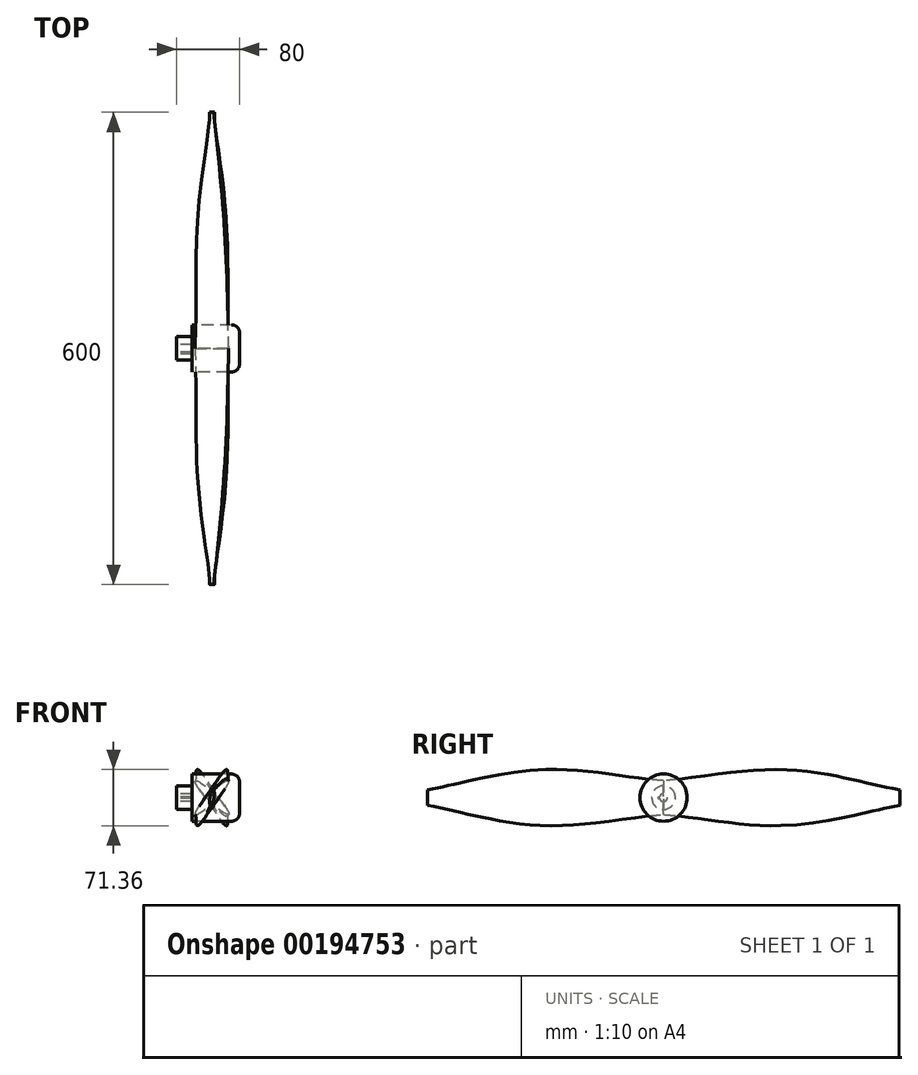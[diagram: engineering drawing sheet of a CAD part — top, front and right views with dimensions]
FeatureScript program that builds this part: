
annotation { "Feature Type Name" : "Feature", "Feature Type Description" : "" }
export const myFeature = defineFeature(function(context is Context, id is Id, definition is map)
    precondition{}
    {
        {
            assignVariable(context, id + "F0", {"name" : "Amplitude", "anyValue" : 300});
        }
        {
            var Q0;
            Q0=qCreatedBy(makeId("Front.planeOp"),FACE);
            var sketch = newSketch(context, id + "F1", { "sketchPlane" : qUnion([Q0])});
            skEllipse(sketch, "E0", {"center": v(0, 0) * mm, "majorRadius": 30 * mm, "minorRadius": 5 * mm, "majorAxis": v(0.7, 0.7)});
            skLineSegment(sketch, "E1", {"start": v(-21.21, -21.21) * mm, "end": v(21.21, 21.21) * mm, "construction": true});
            skLineSegment(sketch, "E2", {"start": v(-3.54, 3.54) * mm, "end": v(3.54, -3.54) * mm, "construction": true});
            skSolve(sketch);
        }
        {
            var Q0;
            Q0=qCreatedBy(makeId("Front.planeOp"),FACE);
            cPlane(context, id + "F2", {"entities" : qUnion([Q0]), "cplaneType" : CPlaneType.OFFSET, "offset" : (getVariable(context, 'Amplitude') / 2) * mm, "width" : 150 * mm, "height" : 150 * mm});
        }
        {
            var Q0;
            Q0=qCreatedBy(id+"F2.planeOp",FACE);
            var sketch = newSketch(context, id + "F3", { "sketchPlane" : qUnion([Q0])});
            skEllipse(sketch, "E3", {"center": v(0, 0) * mm, "majorRadius": 40 * mm, "minorRadius": 5 * mm, "majorAxis": v(0.46, 0.89)});
            skLineSegment(sketch, "E4", {"start": v(-18.47, -35.48) * mm, "end": v(18.47, 35.48) * mm, "construction": true});
            skLineSegment(sketch, "E5", {"start": v(4.44, -2.3) * mm, "end": v(-4.44, 2.3) * mm, "construction": true});
            skSolve(sketch);
        }
        {
            var Q0;
            Q0=qCreatedBy(makeId("Front.planeOp"),FACE);
            cPlane(context, id + "F4", {"entities" : qUnion([Q0]), "cplaneType" : CPlaneType.OFFSET, "offset" : (getVariable(context, 'Amplitude')) * mm, "width" : 150 * mm, "height" : 150 * mm});
        }
        {
            var Q0;
            Q0=qCreatedBy(id+"F4.planeOp",FACE);
            var sketch = newSketch(context, id + "F5", { "sketchPlane" : qUnion([Q0])});
            skEllipse(sketch, "E6", {"center": v(0, 0) * mm, "majorRadius": 10 * mm, "minorRadius": 2.5 * mm, "majorAxis": v(0.17, 0.98)});
            skLineSegment(sketch, "E7", {"start": v(-1.74, -9.85) * mm, "end": v(1.74, 9.85) * mm, "construction": true});
            skLineSegment(sketch, "E8", {"start": v(-2.46, 0.43) * mm, "end": v(2.46, -0.43) * mm, "construction": true});
            skSolve(sketch);
        }
        {
            var Q0;
            Q0 = qSketchRegion(id + "F1", true);
            var Q1;
            Q1 = qSketchRegion(id + "F3", true);
            var Q2;
            Q2 = qSketchRegion(id + "F5", true);
            loft(context, id + "F6", {"sheetProfilesArray" : [{ "sheetProfileEntities" : qUnion([Q0]) }, { "sheetProfileEntities" : qUnion([Q1]) }, { "sheetProfileEntities" : qUnion([Q2]) }]});
        }
        {
            var Q0;
            Q0=qCreatedBy(makeId("Front.planeOp"),FACE);
            var sketch = newSketch(context, id + "F7", { "sketchPlane" : qUnion([Q0])});
            skLineSegment(sketch, "E9", {"start": v(-110.8, 0) * mm, "end": v(122.07, 0) * mm, "construction": true});
            skSolve(sketch);
        }
        {
            var Q0;
            Q0=makeQuery(id+"F6.opLoft","SWEPT_BODY",BODY,{"disambiguationData":[OSD([makeQuery(id+"F1.imprint","IMPRINT",FACE,{"disambiguationData":[TD([[makeQuery(id+"F1.imprint","IMPRINT",EDGE,{"derivedFrom":sQuery(id+"F1.wireOp",EDGE,"E0")}),1.0]])]}),sQuery(id+"F3.wireOp",EDGE,"E3"),makeQuery(id+"F5.imprint","IMPRINT",FACE,{"disambiguationData":[TD([[makeQuery(id+"F5.imprint","IMPRINT",EDGE,{"derivedFrom":sQuery(id+"F5.wireOp",EDGE,"E6")}),1.0]])]})])]});
            var Q1;
            Q1=sQuery(id+"F7.wireOp",EDGE,"E9");
            circularPattern(context, id + "F8", {"entities" : qUnion([Q0]), "axis" : qUnion([Q1]), "angle" : 360 * degree, "instanceCount" : 2, "equalSpace" : true});
        }
        {
            var Q0;
            Q0=qCreatedBy(makeId("Front.planeOp"),FACE);
            var sketch = newSketch(context, id + "F9", { "sketchPlane" : qUnion([Q0])});
            skLineSegment(sketch, "E10", {"start": v(-45, 0) * mm, "end": v(35, 0) * mm});
            skLineSegment(sketch, "E11", {"start": v(35, 0) * mm, "end": v(35, 30) * mm});
            skLineSegment(sketch, "E12", {"start": v(35, 30) * mm, "end": v(-25, 30) * mm});
            skLineSegment(sketch, "E13", {"start": v(-25, 30) * mm, "end": v(-25, 15) * mm});
            skLineSegment(sketch, "E14", {"start": v(-25, 15) * mm, "end": v(-45, 15) * mm});
            skLineSegment(sketch, "E15", {"start": v(-45, 15) * mm, "end": v(-45, 0) * mm});
            skLineSegment(sketch, "E16", {"start": v(-48.47, 0) * mm, "end": v(48.08, 0) * mm, "construction": true});
            skSolve(sketch);
        }
        {
            var Q0;
            Q0 = qSketchRegion(id + "F9", true);
            var Q1;
            Q1=sQuery(id+"F9.wireOp",EDGE,"E16");
            revolve(context, id + "F10", {"entities" : qUnion([Q0]), "axis" : qUnion([Q1]), "revolveType" : RevolveType.FULL});
        }
        {
            var Q0;
            Q0=makeQuery(id+"F10.opRevolve","SWEPT_EDGE",EDGE,{"disambiguationData":[OSD([sQuery(id+"F9.wireOp",EDGE,"E11"),sQuery(id+"F9.wireOp",EDGE,"E12")])]});
            fillet(context, id + "F11", {"entities" : qUnion([Q0]), "radius" : 10 * mm, "tangentPropagation" : true, "allowEdgeOverflow" : false});
        }
        {
            var Q0;
            Q0=makeQuery(id+"F10.opRevolve","SWEPT_FACE",FACE,{"disambiguationData":[OSD([sQuery(id+"F9.wireOp",EDGE,"E15")])]});
            var sketch = newSketch(context, id + "F12", { "sketchPlane" : qUnion([Q0])});
            skArc(sketch, "E17", {"start": v(4.9, 1) * mm, "mid": v(-5, 0) * mm, "end": v(4.9, -1) * mm});
            skLineSegment(sketch, "E18.bottom", {"start": v(6.9, 1) * mm, "end": v(4.9, 1) * mm});
            skLineSegment(sketch, "E18.top", {"start": v(6.9, -1) * mm, "end": v(4.9, -1) * mm});
            skLineSegment(sketch, "E18.left", {"start": v(6.9, 1) * mm, "end": v(6.9, -1) * mm});
            skSolve(sketch);
        }
        {
            var Q0;
            Q0 = qSketchRegion(id + "F12", true);
            extrude(context, id + "F13", {"entities" : qUnion([Q0]), "operationType" : NewBodyOperationType.REMOVE, "oppositeDirection" : true, "depth" : 20 * mm});
        }
    });
